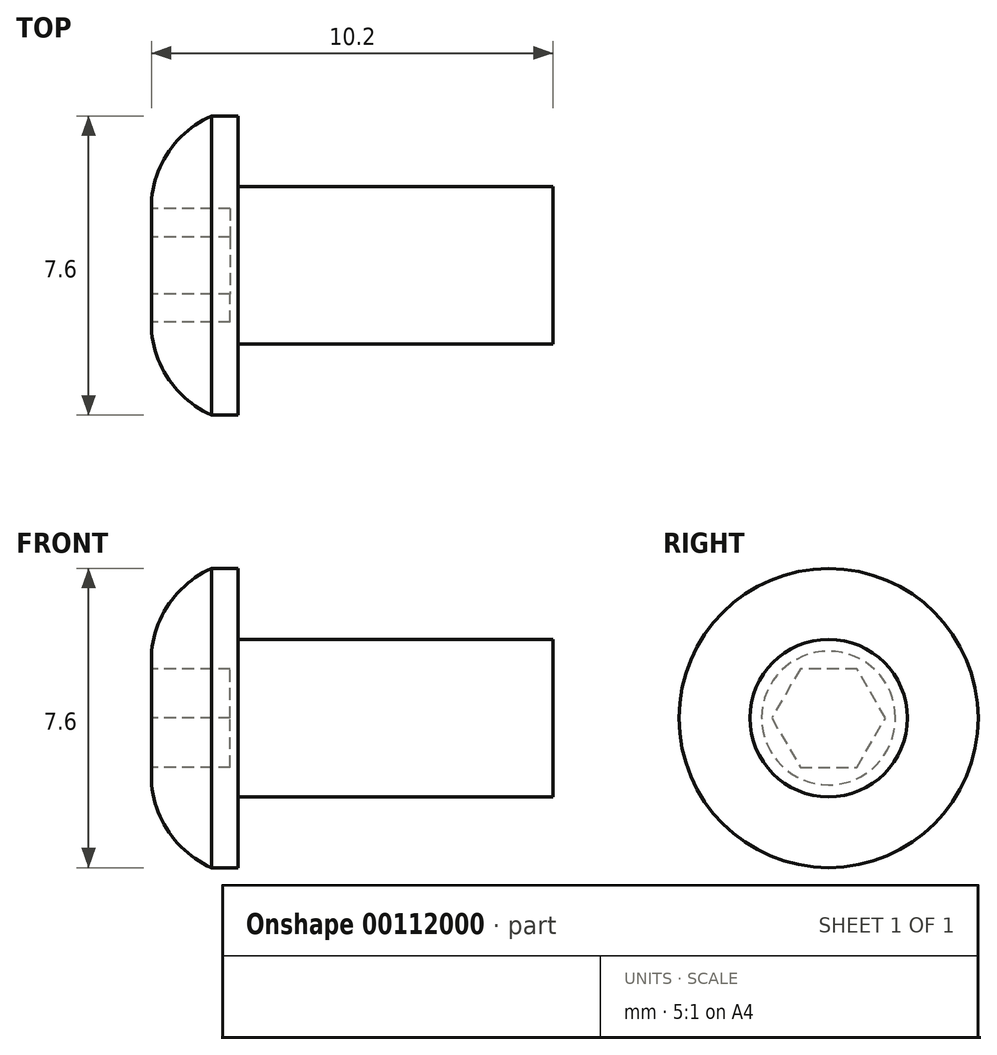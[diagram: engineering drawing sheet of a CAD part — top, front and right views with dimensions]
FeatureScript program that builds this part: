
annotation { "Feature Type Name" : "Feature", "Feature Type Description" : "" }
export const myFeature = defineFeature(function(context is Context, id is Id, definition is map)
    precondition{}
    {
        {
            var Q0;
            Q0=qCreatedBy(makeId("Front.planeOp"),FACE);
            var sketch = newSketch(context, id + "F0", { "sketchPlane" : qUnion([Q0])});
            skLineSegment(sketch, "E0", {"start": v(0, 0) * mm, "end": v(0, 2) * mm});
            skLineSegment(sketch, "E1", {"start": v(0, 2) * mm, "end": v(-8, 2) * mm});
            skLineSegment(sketch, "E2", {"start": v(-8, 2) * mm, "end": v(-8, 3.8) * mm});
            skLineSegment(sketch, "E3", {"start": v(-8, 3.8) * mm, "end": v(-8.68, 3.8) * mm});
            skLineSegment(sketch, "E4", {"start": v(-10.2, 1.7) * mm, "end": v(-10.2, 0) * mm});
            skLineSegment(sketch, "E5", {"start": v(-10.2, 0) * mm, "end": v(0, 0) * mm});
            skArc(sketch, "E6", {"start": v(-8.68, 3.8) * mm, "mid": v(-9.72, 2.95) * mm, "end": v(-10.2, 1.7) * mm});
            skSolve(sketch);
        }
        {
            var Q0;
            Q0 = qSketchRegion(id + "F0", true);
            var Q1;
            Q1=sQuery(id+"F0.wireOp",EDGE,"E5");
            revolve(context, id + "F1", {"entities" : qUnion([Q0]), "axis" : qUnion([Q1]), "revolveType" : RevolveType.FULL});
        }
        {
            var Q0;
            Q0=makeQuery(id+"F1.opRevolve","SWEPT_FACE",FACE,{"disambiguationData":[OSD([sQuery(id+"F0.wireOp",EDGE,"E4")])]});
            var sketch = newSketch(context, id + "F2", { "sketchPlane" : qUnion([Q0])});
            skCircle(sketch, "E7.cCircle", {"center": v(0, 0) * mm, "radius": 1.25 * mm, "construction": true});
            skLineSegment(sketch, "E7.0", {"start": v(-0.72, 1.25) * mm, "end": v(0.72, 1.25) * mm});
            skLineSegment(sketch, "E7.1", {"start": v(0.72, 1.25) * mm, "end": v(1.44, 0) * mm});
            skLineSegment(sketch, "E7.2", {"start": v(1.44, 0) * mm, "end": v(0.72, -1.25) * mm});
            skLineSegment(sketch, "E7.3", {"start": v(0.72, -1.25) * mm, "end": v(-0.72, -1.25) * mm});
            skLineSegment(sketch, "E7.4", {"start": v(-0.72, -1.25) * mm, "end": v(-1.44, 0) * mm});
            skLineSegment(sketch, "E7.5", {"start": v(-1.44, 0) * mm, "end": v(-0.72, 1.25) * mm});
            skPoint(sketch, "E7.0.midPoint", {"position": v(0, 1.25) * mm});
            skSolve(sketch);
        }
        {
            var Q0;
            Q0 = qSketchRegion(id + "F2", true);
            extrude(context, id + "F3", {"entities" : qUnion([Q0]), "operationType" : NewBodyOperationType.REMOVE, "oppositeDirection" : true, "depth" : 2 * mm});
        }
    });
